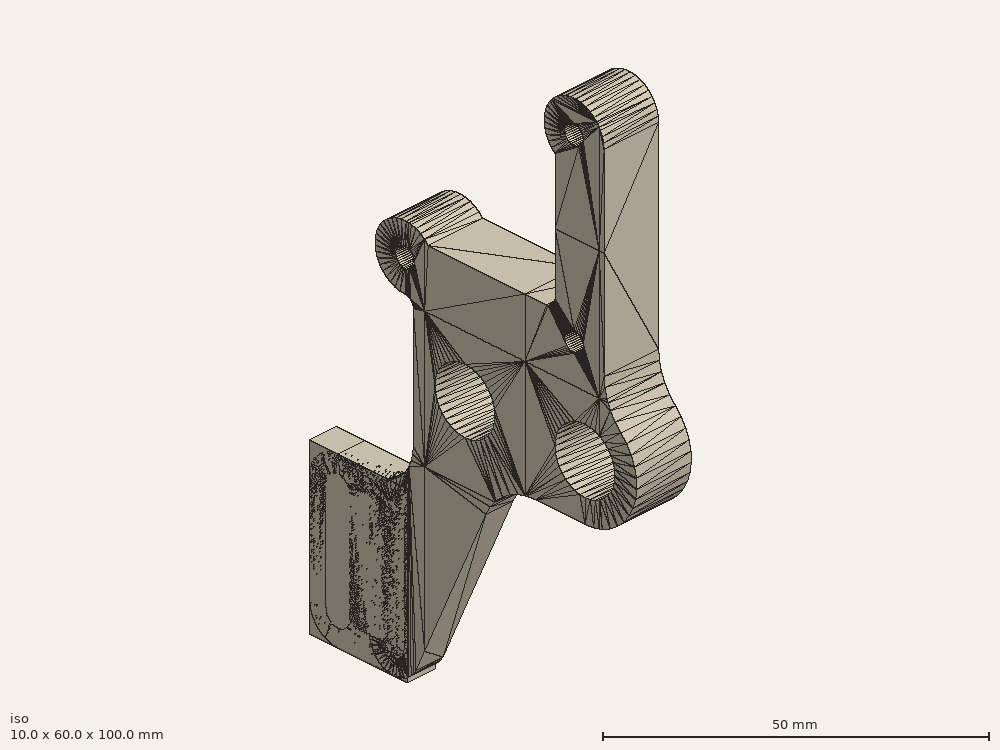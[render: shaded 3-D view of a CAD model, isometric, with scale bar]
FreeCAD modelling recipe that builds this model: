
FCSTD DOCUMENT  (FreeCAD 0.14R3702 (Git))
Label: y-end-motor
License: CC-BY 3.0
LicenseURL: http://creativecommons.org/licenses/by/3.0/
objects: App::MeasureDistance×5, Part::Feature×2, Mesh::Feature×1, Part::Box×1, Sketcher::SketchObject×1, PartDesign::Pocket×1, PartDesign::Fillet×1, Part::MultiFuse×1
note: 8 computed .brp shape members not serialized (recipe doc carries the construction recipe); baked Part::Feature solids carry a one-line shape summary decoded from their .brp

FEATURE [Mesh::Feature] E___Y_Motor_V2  label="E - Y_Motor_V2"
FEATURE [Part::Box] Box  label="Cube"
  Height = 29
  Length = 5
  Placement = pos=(0,42,0) rot=(0,0,1;0rad)
  Width = 18
FEATURE [App::MeasureDistance] Distance  label="Distance: 29.007"
  Distance = 29.0073
  P1 = (5,45.1232,29.0579)
  P2 = (5,44.9164,0.0513545)
FEATURE [App::MeasureDistance] Distance001  label="Distance: 4.925"
  Distance = 4.92459
  P1 = (4.98738,49,4.52893)
  P2 = (0.0627917,49,4.5302)
FEATURE [App::MeasureDistance] Distance002  label="Distance: 3.479"
  Distance = 3.47867
  P1 = (5,42.7469,4.37705)
  P2 = (5,46.2253,4.4183)
FEATURE [App::MeasureDistance] Distance003  label="Distance: 2.656"
  Distance = 2.65585
  P1 = (5,46.2301,4.42636)
  P2 = (5,48.8833,4.54391)
FEATURE [App::MeasureDistance] Distance004  label="Distance: 2.705"
  Distance = 2.70494
  P1 = (5,44.5004,2.78068)
  P2 = (5,44.5844,0.0770435)
FEATURE [Sketcher::SketchObject] Sketch
  ExternalGeometry = -> [Box]
  Placement = pos=(5,42,0) rot=(0.57735,0.57735,0.57735;2.0944rad)
  Support = -> Box [Face2]
  sketch-geometry (10):
    g0: ArcOfCircle CenterX=12.8 CenterY=5.2 CenterZ=0 NormalX=0 NormalY=0 NormalZ=1 Radius=2.2 StartAngle=3.14159 EndAngle=6.28319
    g1: ArcOfCircle CenterX=12.8 CenterY=23.8 CenterZ=0 NormalX=0 NormalY=0 NormalZ=1 Radius=2.2 StartAngle=6.28318 EndAngle=9.42478
    g2: LineSegment StartX=10.6 StartY=23.8 StartZ=0 EndX=10.6 EndY=5.20001 EndZ=0
    g3: LineSegment StartX=15 StartY=23.8 StartZ=0 EndX=15 EndY=5.20001 EndZ=0
    g4: ArcOfCircle CenterX=12.8 CenterY=23.8 CenterZ=0 NormalX=0 NormalY=0 NormalZ=1 Radius=5.2 StartAngle=6.28318 EndAngle=7.85398
    g5: LineSegment StartX=18 StartY=23.8 StartZ=0 EndX=18 EndY=5.20001 EndZ=0
    g6: ArcOfCircle CenterX=12.8 CenterY=5.2 CenterZ=0 NormalX=0 NormalY=0 NormalZ=1 Radius=5.2 StartAngle=4.71239 EndAngle=6.28319
    g7: LineSegment StartX=12.8 StartY=29 StartZ=0 EndX=19 EndY=29 EndZ=0
    g8: LineSegment StartX=19 StartY=29 StartZ=0 EndX=19 EndY=1.2e-11 EndZ=0
    g9: LineSegment StartX=19 StartY=1.1e-11 StartZ=0 EndX=12.8 EndY=1.1e-11 EndZ=0
  constraints (32):
    c: Coincident(g2,g1)
    c: Coincident(g2,g0)
    c: Vertical(g2)
    c: Tangent(g2,g1)
    c: Coincident(g3,g1)
    c: Coincident(g3,g0)
    c: Vertical(g3)
    c: Tangent(g3,g1)
    c: Tangent(g3,g0)
    c: Tangent(g0,g2)
    c: Radius(g1) = 2.2
    c: Coincident(g4,g1)
    c: PointOnObject(g4,g-4)
    c: PointOnObject(g4,g-3)
    c: DistanceX(g1,g4) = 3
    c: Coincident(g5,g4)
    c: Coincident(g6,g0)
    c: PointOnObject(g6,g-4)
    c: Equal(g6,g4)
    c: Coincident(g5,g6)
    c: Tangent(g5,g6)
    c: Tangent(g6,g-1)
    c: PointOnObject(g6,g-1)
    c: Tangent(g4,g-3)
    c: Tangent(g7,g4)
    c: Coincident(g7,g8)
    c: Coincident(g8,g9)
    c: Coincident(g4,g7)
    c: DistanceX(g-4,g7) = 1
    c: Coincident(g9,g6)
    c: Vertical(g8)
    c: Horizontal(g9)
FEATURE [PartDesign::Pocket] Pocket
  Length = 5
  Placement = pos=(0,42,0) rot=(0,0,1;0rad)
  Sketch = -> Sketch
  Type = 0
FEATURE [PartDesign::Fillet] Fillet
  Base = -> Pocket [Edge23]
  Placement = pos=(0,42,0) rot=(0,0,1;0rad)
  Radius = 3
FEATURE [Part::Feature] E___Y_Motor_V2001
  shape: bbox 10 x 48.99 x 99.98 mm, 1952 faces, 0 solids (baked)
FEATURE [Part::Feature] E___Y_Motor_V2001_solid  label="E___Y_Motor_V2001 (Solid)"
  shape: bbox 10 x 48.99 x 99.98 mm, 1952 faces (baked)
FEATURE [Part::MultiFuse] Fusion
  Shapes = -> [Fillet,E___Y_Motor_V2001_solid]
